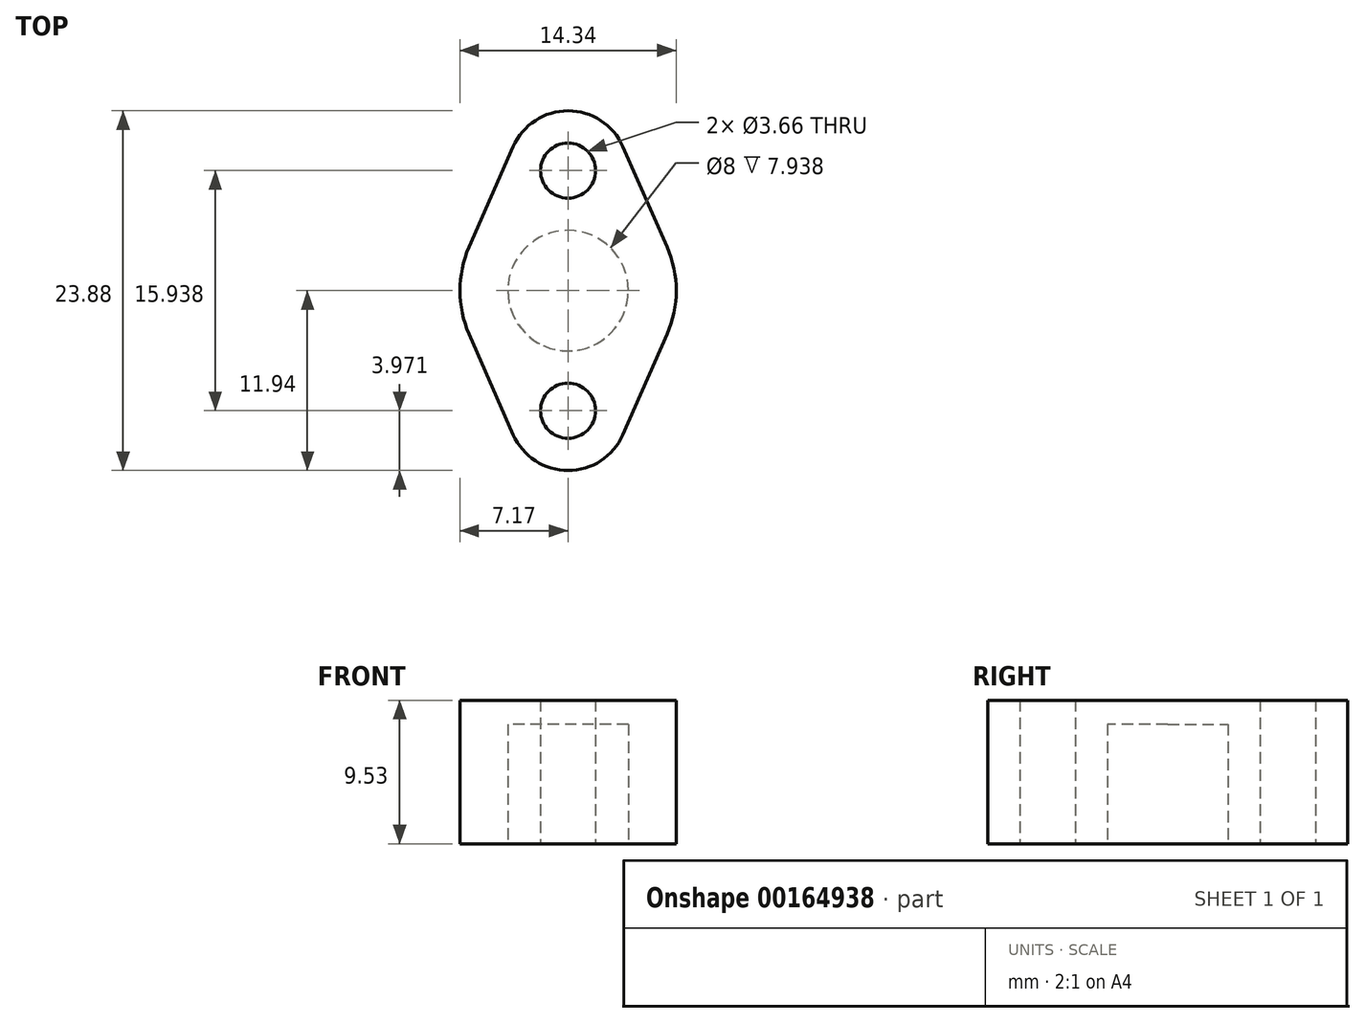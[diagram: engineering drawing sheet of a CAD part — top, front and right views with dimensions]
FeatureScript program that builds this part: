
annotation { "Feature Type Name" : "Feature", "Feature Type Description" : "" }
export const myFeature = defineFeature(function(context is Context, id is Id, definition is map)
    precondition{}
    {
        {
            var Q0;
            Q0=qCreatedBy(makeId("Top.planeOp"),FACE);
            var sketch = newSketch(context, id + "F0", { "sketchPlane" : qUnion([Q0])});
            skCircle(sketch, "E0", {"center": v(0, 0) * mm, "radius": 4 * mm, "construction": true});
            skLineSegment(sketch, "E1", {"start": v(0, 7.97) * mm, "end": v(0, -7.97) * mm, "construction": true});
            skArc(sketch, "E2", {"start": v(3.63, 9.57) * mm, "mid": v(0, 11.94) * mm, "end": v(-3.63, 9.57) * mm});
            skArc(sketch, "E3", {"start": v(-3.63, -9.57) * mm, "mid": v(0, -11.94) * mm, "end": v(3.63, -9.57) * mm});
            skArc(sketch, "E4", {"start": v(3.63, -9.57) * mm, "mid": v(0, -4) * mm, "end": v(-3.63, -9.57) * mm, "construction": true});
            skArc(sketch, "E5", {"start": v(6.57, -2.89) * mm, "mid": v(7.18, 0) * mm, "end": v(6.57, 2.89) * mm});
            skArc(sketch, "E6", {"start": v(-6.57, 2.89) * mm, "mid": v(-7.18, 0) * mm, "end": v(-6.57, -2.89) * mm});
            skLineSegment(sketch, "E7", {"start": v(6.57, -2.89) * mm, "end": v(3.63, -9.57) * mm});
            skLineSegment(sketch, "E8", {"start": v(6.57, 2.89) * mm, "end": v(3.63, 9.57) * mm});
            skLineSegment(sketch, "E9", {"start": v(-3.63, 9.57) * mm, "end": v(-6.57, 2.89) * mm});
            skLineSegment(sketch, "E10", {"start": v(-6.57, -2.89) * mm, "end": v(-3.63, -9.57) * mm});
            skCircle(sketch, "E11", {"center": v(0, 7.97) * mm, "radius": 1.83 * mm});
            skCircle(sketch, "E12", {"center": v(0, -7.97) * mm, "radius": 1.83 * mm});
            skSolve(sketch);
        }
        {
            var Q0;
            Q0 = qSketchRegion(id + "F0", true);
            extrude(context, id + "F1", {"entities" : qUnion([Q0]), "depth" : 9.52 * mm});
        }
        {
            var Q0;
            Q0=makeQuery(id+"F1.opExtrude","CAP_FACE",FACE,{"disambiguationData":[OSD([sQuery(id+"F0.wireOp",EDGE,"E2"),sQuery(id+"F0.wireOp",EDGE,"E3"),sQuery(id+"F0.wireOp",EDGE,"E5"),sQuery(id+"F0.wireOp",EDGE,"E6"),sQuery(id+"F0.wireOp",EDGE,"E7"),sQuery(id+"F0.wireOp",EDGE,"E8"),sQuery(id+"F0.wireOp",EDGE,"E9"),sQuery(id+"F0.wireOp",EDGE,"E10"),sQuery(id+"F0.wireOp",EDGE,"E11"),sQuery(id+"F0.wireOp",EDGE,"E12")])],"isStart":false});
            cPlane(context, id + "F2", {"entities" : qUnion([Q0]), "cplaneType" : CPlaneType.OFFSET, "offset" : 1.59 * mm, "oppositeDirection" : true, "width" : 152.4 * mm, "height" : 152.4 * mm});
        }
        {
            var Q0;
            Q0=makeQuery(id+"F1.opExtrude","CAP_FACE",FACE,{"disambiguationData":[OSD([sQuery(id+"F0.wireOp",EDGE,"E2"),sQuery(id+"F0.wireOp",EDGE,"E3"),sQuery(id+"F0.wireOp",EDGE,"E5"),sQuery(id+"F0.wireOp",EDGE,"E6"),sQuery(id+"F0.wireOp",EDGE,"E7"),sQuery(id+"F0.wireOp",EDGE,"E8"),sQuery(id+"F0.wireOp",EDGE,"E9"),sQuery(id+"F0.wireOp",EDGE,"E10"),sQuery(id+"F0.wireOp",EDGE,"E11"),sQuery(id+"F0.wireOp",EDGE,"E12")])],"isStart":true});
            var sketch = newSketch(context, id + "F3", { "sketchPlane" : qUnion([Q0])});
            skCircle(sketch, "E13", {"center": v(0, 0) * mm, "radius": 4 * mm});
            skSolve(sketch);
        }
        {
            var Q0;
            Q0 = qSketchRegion(id + "F3", true);
            var Q1;
            Q1=qCreatedBy(id+"F2.planeOp",FACE);
            extrude(context, id + "F4", {"entities" : qUnion([Q0]), "operationType" : NewBodyOperationType.REMOVE, "endBound" : BoundingType.UP_TO_SURFACE, "oppositeDirection" : true, "endBoundEntityFace" : qUnion([Q1]), "depth" : 25.4 * mm});
        }
    });
